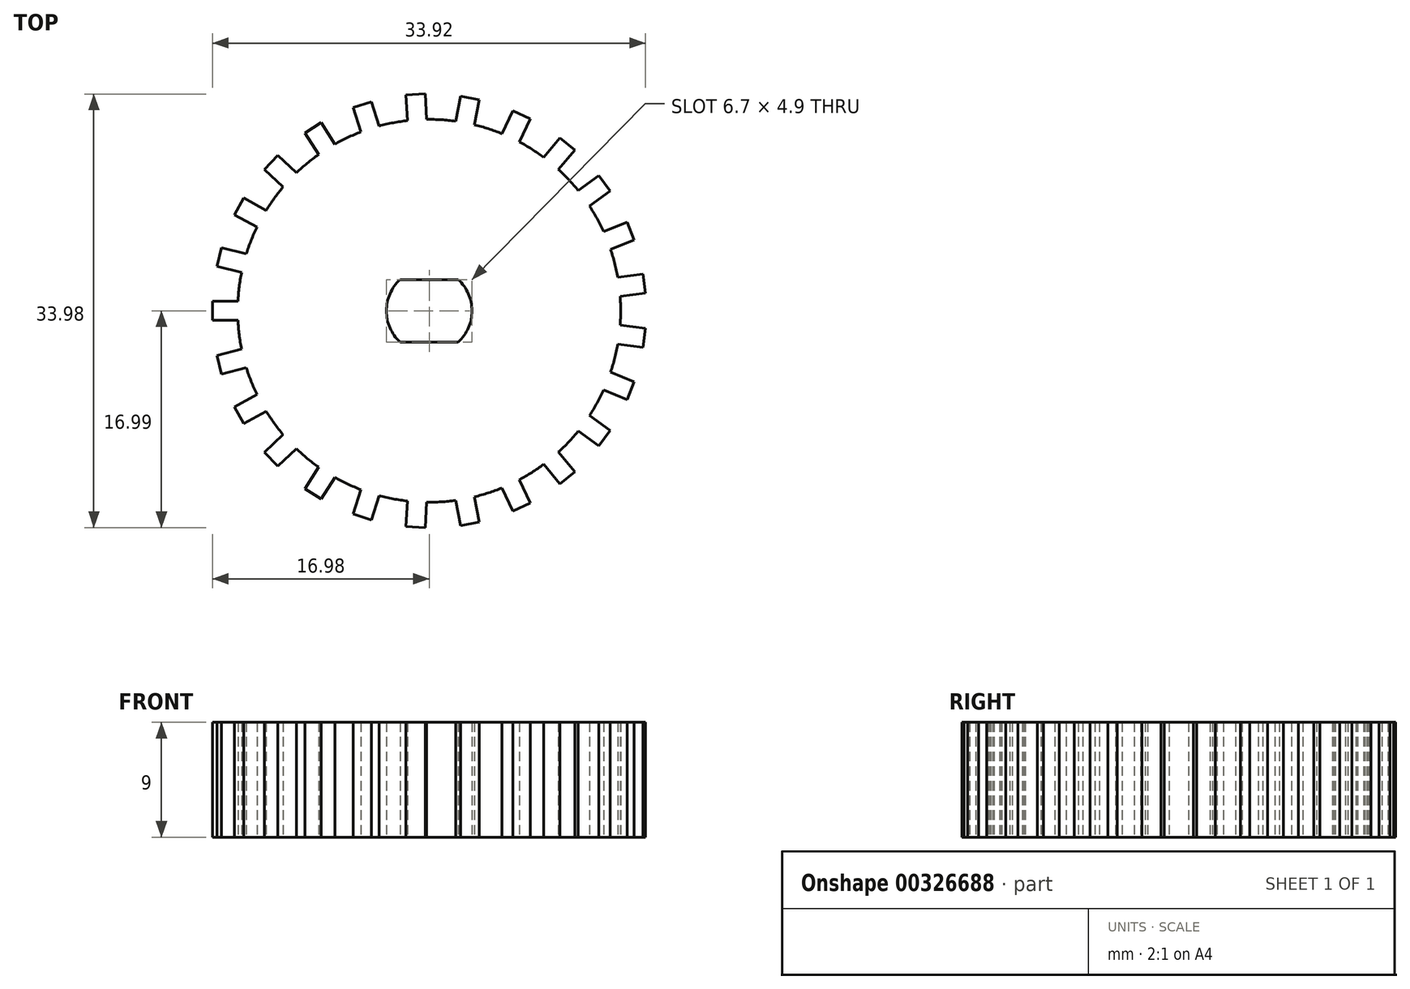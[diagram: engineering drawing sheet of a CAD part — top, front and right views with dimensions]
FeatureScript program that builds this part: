
annotation { "Feature Type Name" : "Feature", "Feature Type Description" : "" }
export const myFeature = defineFeature(function(context is Context, id is Id, definition is map)
    precondition{}
    {
        {
            var Q0;
            Q0=qCreatedBy(makeId("Top.planeOp"),FACE);
            var sketch = newSketch(context, id + "F0", { "sketchPlane" : qUnion([Q0])});
            skArc(sketch, "E0", {"start": v(-2.28, 2.45) * mm, "mid": v(-3.35, 0) * mm, "end": v(-2.28, -2.45) * mm});
            skLineSegment(sketch, "E1.bottom", {"start": v(2.28, -2.45) * mm, "end": v(-2.28, -2.45) * mm});
            skLineSegment(sketch, "E1.top", {"start": v(2.28, 2.45) * mm, "end": v(-2.28, 2.45) * mm});
            skArc(sketch, "E2.trimOffspring", {"start": v(2.28, -2.45) * mm, "mid": v(3.35, 0) * mm, "end": v(2.28, 2.45) * mm});
            skPoint(sketch, "E3.orphan", {"position": v(3.35, 2.45) * mm});
            skPoint(sketch, "E4.orphan", {"position": v(3.35, -2.45) * mm});
            skPoint(sketch, "E5.orphan", {"position": v(-3.35, -2.45) * mm});
            skPoint(sketch, "E6.orphan", {"position": v(-3.35, 2.45) * mm});
            skCircle(sketch, "E7", {"center": v(0, 0) * mm, "radius": 15 * mm});
            skLineSegment(sketch, "E8", {"start": v(-14.98, -0.75) * mm, "end": v(-16.98, -0.75) * mm});
            skLineSegment(sketch, "E9", {"start": v(-16.98, -0.75) * mm, "end": v(-16.98, 0.75) * mm});
            skLineSegment(sketch, "E10", {"start": v(-16.98, 0.75) * mm, "end": v(-14.98, 0.75) * mm});
            skPoint(sketch, "E11", {"position": v(-14.7, 2.95) * mm});
            skPoint(sketch, "E12.1.0", {"position": v(-14.98, -0.8) * mm});
            skLineSegment(sketch, "E12.1.1", {"start": v(-16.63, -3.5) * mm, "end": v(-14.7, -3) * mm});
            skLineSegment(sketch, "E12.1.2", {"start": v(-16.26, -4.95) * mm, "end": v(-16.63, -3.5) * mm});
            skLineSegment(sketch, "E12.1.3", {"start": v(-14.32, -4.45) * mm, "end": v(-16.26, -4.95) * mm});
            skPoint(sketch, "E12.2.0", {"position": v(-14.3, -4.5) * mm});
            skLineSegment(sketch, "E12.2.1", {"start": v(-15.24, -7.52) * mm, "end": v(-13.49, -6.56) * mm});
            skLineSegment(sketch, "E12.2.2", {"start": v(-14.52, -8.84) * mm, "end": v(-15.24, -7.52) * mm});
            skLineSegment(sketch, "E12.2.3", {"start": v(-12.77, -7.87) * mm, "end": v(-14.52, -8.84) * mm});
            skPoint(sketch, "E12.3.0", {"position": v(-12.74, -7.92) * mm});
            skLineSegment(sketch, "E12.3.1", {"start": v(-12.9, -11.08) * mm, "end": v(-11.43, -9.7) * mm});
            skLineSegment(sketch, "E12.3.2", {"start": v(-11.87, -12.17) * mm, "end": v(-12.9, -11.08) * mm});
            skLineSegment(sketch, "E12.3.3", {"start": v(-10.4, -10.8) * mm, "end": v(-11.87, -12.17) * mm});
            skPoint(sketch, "E12.4.0", {"position": v(-10.37, -10.84) * mm});
            skLineSegment(sketch, "E12.4.1", {"start": v(-9.73, -13.94) * mm, "end": v(-8.66, -12.25) * mm});
            skLineSegment(sketch, "E12.4.2", {"start": v(-8.47, -14.74) * mm, "end": v(-9.73, -13.94) * mm});
            skLineSegment(sketch, "E12.4.3", {"start": v(-7.4, -13.05) * mm, "end": v(-8.47, -14.74) * mm});
            skPoint(sketch, "E12.5.0", {"position": v(-7.35, -13.08) * mm});
            skLineSegment(sketch, "E12.5.1", {"start": v(-5.96, -15.92) * mm, "end": v(-5.34, -14.02) * mm});
            skLineSegment(sketch, "E12.5.2", {"start": v(-4.53, -16.38) * mm, "end": v(-5.96, -15.92) * mm});
            skLineSegment(sketch, "E12.5.3", {"start": v(-3.92, -14.48) * mm, "end": v(-4.53, -16.38) * mm});
            skPoint(sketch, "E12.6.0", {"position": v(-3.87, -14.5) * mm});
            skLineSegment(sketch, "E12.6.1", {"start": v(-1.81, -16.9) * mm, "end": v(-1.69, -14.9) * mm});
            skLineSegment(sketch, "E12.6.2", {"start": v(-0.32, -17) * mm, "end": v(-1.81, -16.9) * mm});
            skLineSegment(sketch, "E12.6.3", {"start": v(-0.2, -15) * mm, "end": v(-0.32, -17) * mm});
            skPoint(sketch, "E12.7.0", {"position": v(-0.14, -15) * mm});
            skLineSegment(sketch, "E12.7.1", {"start": v(2.45, -16.82) * mm, "end": v(2.07, -14.86) * mm});
            skLineSegment(sketch, "E12.7.2", {"start": v(3.92, -16.54) * mm, "end": v(2.45, -16.82) * mm});
            skLineSegment(sketch, "E12.7.3", {"start": v(3.54, -14.58) * mm, "end": v(3.92, -16.54) * mm});
            skPoint(sketch, "E12.8.0", {"position": v(3.6, -14.56) * mm});
            skLineSegment(sketch, "E12.8.1", {"start": v(6.55, -15.68) * mm, "end": v(5.7, -13.87) * mm});
            skLineSegment(sketch, "E12.8.2", {"start": v(7.9, -15.05) * mm, "end": v(6.55, -15.68) * mm});
            skLineSegment(sketch, "E12.8.3", {"start": v(7.06, -13.24) * mm, "end": v(7.9, -15.05) * mm});
            skPoint(sketch, "E12.9.0", {"position": v(7.1, -13.21) * mm});
            skLineSegment(sketch, "E12.9.1", {"start": v(10.25, -13.56) * mm, "end": v(8.97, -12.02) * mm});
            skLineSegment(sketch, "E12.9.2", {"start": v(11.4, -12.6) * mm, "end": v(10.25, -13.56) * mm});
            skLineSegment(sketch, "E12.9.3", {"start": v(10.13, -11.07) * mm, "end": v(11.4, -12.6) * mm});
            skPoint(sketch, "E12.10.0", {"position": v(10.16, -11.03) * mm});
            skLineSegment(sketch, "E12.10.1", {"start": v(13.3, -10.59) * mm, "end": v(11.68, -9.41) * mm});
            skLineSegment(sketch, "E12.10.2", {"start": v(14.18, -9.37) * mm, "end": v(13.3, -10.59) * mm});
            skLineSegment(sketch, "E12.10.3", {"start": v(12.56, -8.2) * mm, "end": v(14.18, -9.37) * mm});
            skPoint(sketch, "E12.11.0", {"position": v(12.59, -8.16) * mm});
            skLineSegment(sketch, "E12.11.1", {"start": v(15.51, -6.95) * mm, "end": v(13.65, -6.21) * mm});
            skLineSegment(sketch, "E12.11.2", {"start": v(16.06, -5.55) * mm, "end": v(15.51, -6.95) * mm});
            skLineSegment(sketch, "E12.11.3", {"start": v(14.2, -4.82) * mm, "end": v(16.06, -5.55) * mm});
            skPoint(sketch, "E12.12.0", {"position": v(14.22, -4.77) * mm});
            skLineSegment(sketch, "E12.12.1", {"start": v(16.75, -2.87) * mm, "end": v(14.77, -2.62) * mm});
            skLineSegment(sketch, "E12.12.2", {"start": v(16.94, -1.38) * mm, "end": v(16.75, -2.87) * mm});
            skLineSegment(sketch, "E12.12.3", {"start": v(14.96, -1.13) * mm, "end": v(16.94, -1.38) * mm});
            skPoint(sketch, "E12.13.0", {"position": v(14.96, -1.08) * mm});
            skLineSegment(sketch, "E12.13.1", {"start": v(16.94, 1.38) * mm, "end": v(14.96, 1.13) * mm});
            skLineSegment(sketch, "E12.13.2", {"start": v(16.75, 2.87) * mm, "end": v(16.94, 1.38) * mm});
            skLineSegment(sketch, "E12.13.3", {"start": v(14.77, 2.62) * mm, "end": v(16.75, 2.87) * mm});
            skPoint(sketch, "E12.14.0", {"position": v(14.76, 2.67) * mm});
            skLineSegment(sketch, "E12.14.1", {"start": v(16.06, 5.55) * mm, "end": v(14.2, 4.82) * mm});
            skLineSegment(sketch, "E12.14.2", {"start": v(15.51, 6.95) * mm, "end": v(16.06, 5.55) * mm});
            skLineSegment(sketch, "E12.14.3", {"start": v(13.65, 6.21) * mm, "end": v(15.51, 6.95) * mm});
            skPoint(sketch, "E12.15.0", {"position": v(13.63, 6.26) * mm});
            skLineSegment(sketch, "E12.15.1", {"start": v(14.18, 9.37) * mm, "end": v(12.56, 8.2) * mm});
            skLineSegment(sketch, "E12.15.2", {"start": v(13.3, 10.59) * mm, "end": v(14.18, 9.37) * mm});
            skLineSegment(sketch, "E12.15.3", {"start": v(11.68, 9.41) * mm, "end": v(13.3, 10.59) * mm});
            skPoint(sketch, "E12.16.0", {"position": v(11.65, 9.45) * mm});
            skLineSegment(sketch, "E12.16.1", {"start": v(11.4, 12.6) * mm, "end": v(10.13, 11.07) * mm});
            skLineSegment(sketch, "E12.16.2", {"start": v(10.25, 13.56) * mm, "end": v(11.4, 12.6) * mm});
            skLineSegment(sketch, "E12.16.3", {"start": v(8.97, 12.02) * mm, "end": v(10.25, 13.56) * mm});
            skPoint(sketch, "E12.17.0", {"position": v(8.93, 12.05) * mm});
            skLineSegment(sketch, "E12.17.1", {"start": v(7.9, 15.05) * mm, "end": v(7.06, 13.24) * mm});
            skLineSegment(sketch, "E12.17.2", {"start": v(6.55, 15.68) * mm, "end": v(7.9, 15.05) * mm});
            skLineSegment(sketch, "E12.17.3", {"start": v(5.7, 13.87) * mm, "end": v(6.55, 15.68) * mm});
            skPoint(sketch, "E12.18.0", {"position": v(5.65, 13.9) * mm});
            skLineSegment(sketch, "E12.18.1", {"start": v(3.92, 16.54) * mm, "end": v(3.54, 14.58) * mm});
            skLineSegment(sketch, "E12.18.2", {"start": v(2.45, 16.82) * mm, "end": v(3.92, 16.54) * mm});
            skLineSegment(sketch, "E12.18.3", {"start": v(2.07, 14.86) * mm, "end": v(2.45, 16.82) * mm});
            skPoint(sketch, "E12.19.0", {"position": v(2.02, 14.86) * mm});
            skLineSegment(sketch, "E12.19.1", {"start": v(-0.32, 17) * mm, "end": v(-0.2, 15) * mm});
            skLineSegment(sketch, "E12.19.2", {"start": v(-1.81, 16.9) * mm, "end": v(-0.32, 17) * mm});
            skLineSegment(sketch, "E12.19.3", {"start": v(-1.69, 14.9) * mm, "end": v(-1.81, 16.9) * mm});
            skPoint(sketch, "E13.0.20.0", {"position": v(-1.74, 14.9) * mm});
            skLineSegment(sketch, "E13.1.20.0", {"start": v(-4.53, 16.38) * mm, "end": v(-3.92, 14.48) * mm});
            skLineSegment(sketch, "E13.4.20.0", {"start": v(-5.96, 15.92) * mm, "end": v(-4.53, 16.38) * mm});
            skLineSegment(sketch, "E13.7.20.0", {"start": v(-5.34, 14.02) * mm, "end": v(-5.96, 15.92) * mm});
            skPoint(sketch, "E14.0.21.0", {"position": v(-5.39, 14) * mm});
            skLineSegment(sketch, "E14.1.21.0", {"start": v(-8.47, 14.74) * mm, "end": v(-7.4, 13.05) * mm});
            skLineSegment(sketch, "E14.4.21.0", {"start": v(-9.73, 13.94) * mm, "end": v(-8.47, 14.74) * mm});
            skLineSegment(sketch, "E14.7.21.0", {"start": v(-8.66, 12.25) * mm, "end": v(-9.73, 13.94) * mm});
            skPoint(sketch, "E15.0.22.0", {"position": v(-8.7, 12.22) * mm});
            skLineSegment(sketch, "E15.1.22.0", {"start": v(-11.87, 12.17) * mm, "end": v(-10.4, 10.8) * mm});
            skLineSegment(sketch, "E15.4.22.0", {"start": v(-12.9, 11.08) * mm, "end": v(-11.87, 12.17) * mm});
            skLineSegment(sketch, "E15.7.22.0", {"start": v(-11.43, 9.7) * mm, "end": v(-12.9, 11.08) * mm});
            skPoint(sketch, "E15.0.23.0", {"position": v(-11.47, 9.67) * mm});
            skLineSegment(sketch, "E15.1.23.0", {"start": v(-14.52, 8.84) * mm, "end": v(-12.77, 7.87) * mm});
            skLineSegment(sketch, "E15.4.23.0", {"start": v(-15.24, 7.52) * mm, "end": v(-14.52, 8.84) * mm});
            skLineSegment(sketch, "E15.7.23.0", {"start": v(-13.49, 6.56) * mm, "end": v(-15.24, 7.52) * mm});
            skPoint(sketch, "E16.0.24.0", {"position": v(-13.51, 6.51) * mm});
            skLineSegment(sketch, "E16.1.24.0", {"start": v(-16.26, 4.95) * mm, "end": v(-14.32, 4.45) * mm});
            skLineSegment(sketch, "E16.4.24.0", {"start": v(-16.63, 3.5) * mm, "end": v(-16.26, 4.95) * mm});
            skLineSegment(sketch, "E16.7.24.0", {"start": v(-14.7, 3) * mm, "end": v(-16.63, 3.5) * mm});
            skSolve(sketch);
        }
        {
            var Q0;
            {var subQ0=sQuery(id+"F0.wireOp",EDGE,"E16.1.24.0");Q0=makeQuery(id+"F0.imprint","IMPRINT",FACE,{"disambiguationData":[TD([[makeQuery(id+"F0.imprint","IMPRINT",EDGE,{"derivedFrom":subQ0}),-1.0]])]});}
            var Q1;
            {var subQ0=sQuery(id+"F0.wireOp",EDGE,"E15.1.23.0");Q1=makeQuery(id+"F0.imprint","IMPRINT",FACE,{"disambiguationData":[TD([[makeQuery(id+"F0.imprint","IMPRINT",EDGE,{"derivedFrom":subQ0}),-1.0]])]});}
            var Q2;
            {var subQ0=sQuery(id+"F0.wireOp",EDGE,"E15.1.22.0");Q2=makeQuery(id+"F0.imprint","IMPRINT",FACE,{"disambiguationData":[TD([[makeQuery(id+"F0.imprint","IMPRINT",EDGE,{"derivedFrom":subQ0}),-1.0]])]});}
            var Q3;
            {var subQ0=sQuery(id+"F0.wireOp",EDGE,"E14.1.21.0");Q3=makeQuery(id+"F0.imprint","IMPRINT",FACE,{"disambiguationData":[TD([[makeQuery(id+"F0.imprint","IMPRINT",EDGE,{"derivedFrom":subQ0}),-1.0]])]});}
            var Q4;
            {var subQ0=sQuery(id+"F0.wireOp",EDGE,"E8");Q4=makeQuery(id+"F0.imprint","IMPRINT",FACE,{"disambiguationData":[TD([[makeQuery(id+"F0.imprint","IMPRINT",EDGE,{"derivedFrom":subQ0}),-1.0]])]});}
            var Q5;
            {var subQ0=sQuery(id+"F0.wireOp",EDGE,"E12.1.1");Q5=makeQuery(id+"F0.imprint","IMPRINT",FACE,{"disambiguationData":[TD([[makeQuery(id+"F0.imprint","IMPRINT",EDGE,{"derivedFrom":subQ0}),-1.0]])]});}
            var Q6;
            {var subQ0=sQuery(id+"F0.wireOp",EDGE,"E12.2.1");Q6=makeQuery(id+"F0.imprint","IMPRINT",FACE,{"disambiguationData":[TD([[makeQuery(id+"F0.imprint","IMPRINT",EDGE,{"derivedFrom":subQ0}),-1.0]])]});}
            var Q7;
            Q7=makeQuery(id+"F0.imprint","IMPRINT",FACE,{"disambiguationData":[TD([[makeQuery(id+"F0.imprint","IMPRINT",EDGE,{"derivedFrom":sQuery(id+"F0.wireOp",EDGE,"E0")}),-1.0]])]});
            var Q8;
            {var subQ0=sQuery(id+"F0.wireOp",EDGE,"E12.3.1");Q8=makeQuery(id+"F0.imprint","IMPRINT",FACE,{"disambiguationData":[TD([[makeQuery(id+"F0.imprint","IMPRINT",EDGE,{"derivedFrom":subQ0}),-1.0]])]});}
            var Q9;
            {var subQ0=sQuery(id+"F0.wireOp",EDGE,"E12.4.1");Q9=makeQuery(id+"F0.imprint","IMPRINT",FACE,{"disambiguationData":[TD([[makeQuery(id+"F0.imprint","IMPRINT",EDGE,{"derivedFrom":subQ0}),-1.0]])]});}
            var Q10;
            {var subQ0=sQuery(id+"F0.wireOp",EDGE,"E13.1.20.0");Q10=makeQuery(id+"F0.imprint","IMPRINT",FACE,{"disambiguationData":[TD([[makeQuery(id+"F0.imprint","IMPRINT",EDGE,{"derivedFrom":subQ0}),-1.0]])]});}
            var Q11;
            {var subQ0=sQuery(id+"F0.wireOp",EDGE,"E12.19.1");Q11=makeQuery(id+"F0.imprint","IMPRINT",FACE,{"disambiguationData":[TD([[makeQuery(id+"F0.imprint","IMPRINT",EDGE,{"derivedFrom":subQ0}),-1.0]])]});}
            var Q12;
            {var subQ0=sQuery(id+"F0.wireOp",EDGE,"E12.18.1");Q12=makeQuery(id+"F0.imprint","IMPRINT",FACE,{"disambiguationData":[TD([[makeQuery(id+"F0.imprint","IMPRINT",EDGE,{"derivedFrom":subQ0}),-1.0]])]});}
            var Q13;
            {var subQ0=sQuery(id+"F0.wireOp",EDGE,"E12.17.1");Q13=makeQuery(id+"F0.imprint","IMPRINT",FACE,{"disambiguationData":[TD([[makeQuery(id+"F0.imprint","IMPRINT",EDGE,{"derivedFrom":subQ0}),-1.0]])]});}
            var Q14;
            {var subQ0=sQuery(id+"F0.wireOp",EDGE,"E12.16.1");Q14=makeQuery(id+"F0.imprint","IMPRINT",FACE,{"disambiguationData":[TD([[makeQuery(id+"F0.imprint","IMPRINT",EDGE,{"derivedFrom":subQ0}),-1.0]])]});}
            var Q15;
            {var subQ0=sQuery(id+"F0.wireOp",EDGE,"E12.15.1");Q15=makeQuery(id+"F0.imprint","IMPRINT",FACE,{"disambiguationData":[TD([[makeQuery(id+"F0.imprint","IMPRINT",EDGE,{"derivedFrom":subQ0}),-1.0]])]});}
            var Q16;
            {var subQ0=sQuery(id+"F0.wireOp",EDGE,"E12.14.1");Q16=makeQuery(id+"F0.imprint","IMPRINT",FACE,{"disambiguationData":[TD([[makeQuery(id+"F0.imprint","IMPRINT",EDGE,{"derivedFrom":subQ0}),-1.0]])]});}
            var Q17;
            {var subQ0=sQuery(id+"F0.wireOp",EDGE,"E12.13.1");Q17=makeQuery(id+"F0.imprint","IMPRINT",FACE,{"disambiguationData":[TD([[makeQuery(id+"F0.imprint","IMPRINT",EDGE,{"derivedFrom":subQ0}),-1.0]])]});}
            var Q18;
            {var subQ0=sQuery(id+"F0.wireOp",EDGE,"E12.12.1");Q18=makeQuery(id+"F0.imprint","IMPRINT",FACE,{"disambiguationData":[TD([[makeQuery(id+"F0.imprint","IMPRINT",EDGE,{"derivedFrom":subQ0}),-1.0]])]});}
            var Q19;
            {var subQ0=sQuery(id+"F0.wireOp",EDGE,"E12.11.1");Q19=makeQuery(id+"F0.imprint","IMPRINT",FACE,{"disambiguationData":[TD([[makeQuery(id+"F0.imprint","IMPRINT",EDGE,{"derivedFrom":subQ0}),-1.0]])]});}
            var Q20;
            {var subQ0=sQuery(id+"F0.wireOp",EDGE,"E12.10.1");Q20=makeQuery(id+"F0.imprint","IMPRINT",FACE,{"disambiguationData":[TD([[makeQuery(id+"F0.imprint","IMPRINT",EDGE,{"derivedFrom":subQ0}),-1.0]])]});}
            var Q21;
            {var subQ0=sQuery(id+"F0.wireOp",EDGE,"E12.9.1");Q21=makeQuery(id+"F0.imprint","IMPRINT",FACE,{"disambiguationData":[TD([[makeQuery(id+"F0.imprint","IMPRINT",EDGE,{"derivedFrom":subQ0}),-1.0]])]});}
            var Q22;
            {var subQ0=sQuery(id+"F0.wireOp",EDGE,"E12.8.1");Q22=makeQuery(id+"F0.imprint","IMPRINT",FACE,{"disambiguationData":[TD([[makeQuery(id+"F0.imprint","IMPRINT",EDGE,{"derivedFrom":subQ0}),-1.0]])]});}
            var Q23;
            {var subQ0=sQuery(id+"F0.wireOp",EDGE,"E12.7.1");Q23=makeQuery(id+"F0.imprint","IMPRINT",FACE,{"disambiguationData":[TD([[makeQuery(id+"F0.imprint","IMPRINT",EDGE,{"derivedFrom":subQ0}),-1.0]])]});}
            var Q24;
            {var subQ0=sQuery(id+"F0.wireOp",EDGE,"E12.6.1");Q24=makeQuery(id+"F0.imprint","IMPRINT",FACE,{"disambiguationData":[TD([[makeQuery(id+"F0.imprint","IMPRINT",EDGE,{"derivedFrom":subQ0}),-1.0]])]});}
            var Q25;
            {var subQ0=sQuery(id+"F0.wireOp",EDGE,"E12.5.1");Q25=makeQuery(id+"F0.imprint","IMPRINT",FACE,{"disambiguationData":[TD([[makeQuery(id+"F0.imprint","IMPRINT",EDGE,{"derivedFrom":subQ0}),-1.0]])]});}
            extrude(context, id + "F1", {"entities" : qUnion([Q0, Q1, Q2, Q3, Q4, Q5, Q6, Q7, Q8, Q9, Q10, Q11, Q12, Q13, Q14, Q15, Q16, Q17, Q18, Q19, Q20, Q21, Q22, Q23, Q24, Q25]), "depth" : 9 * mm});
        }
    });
